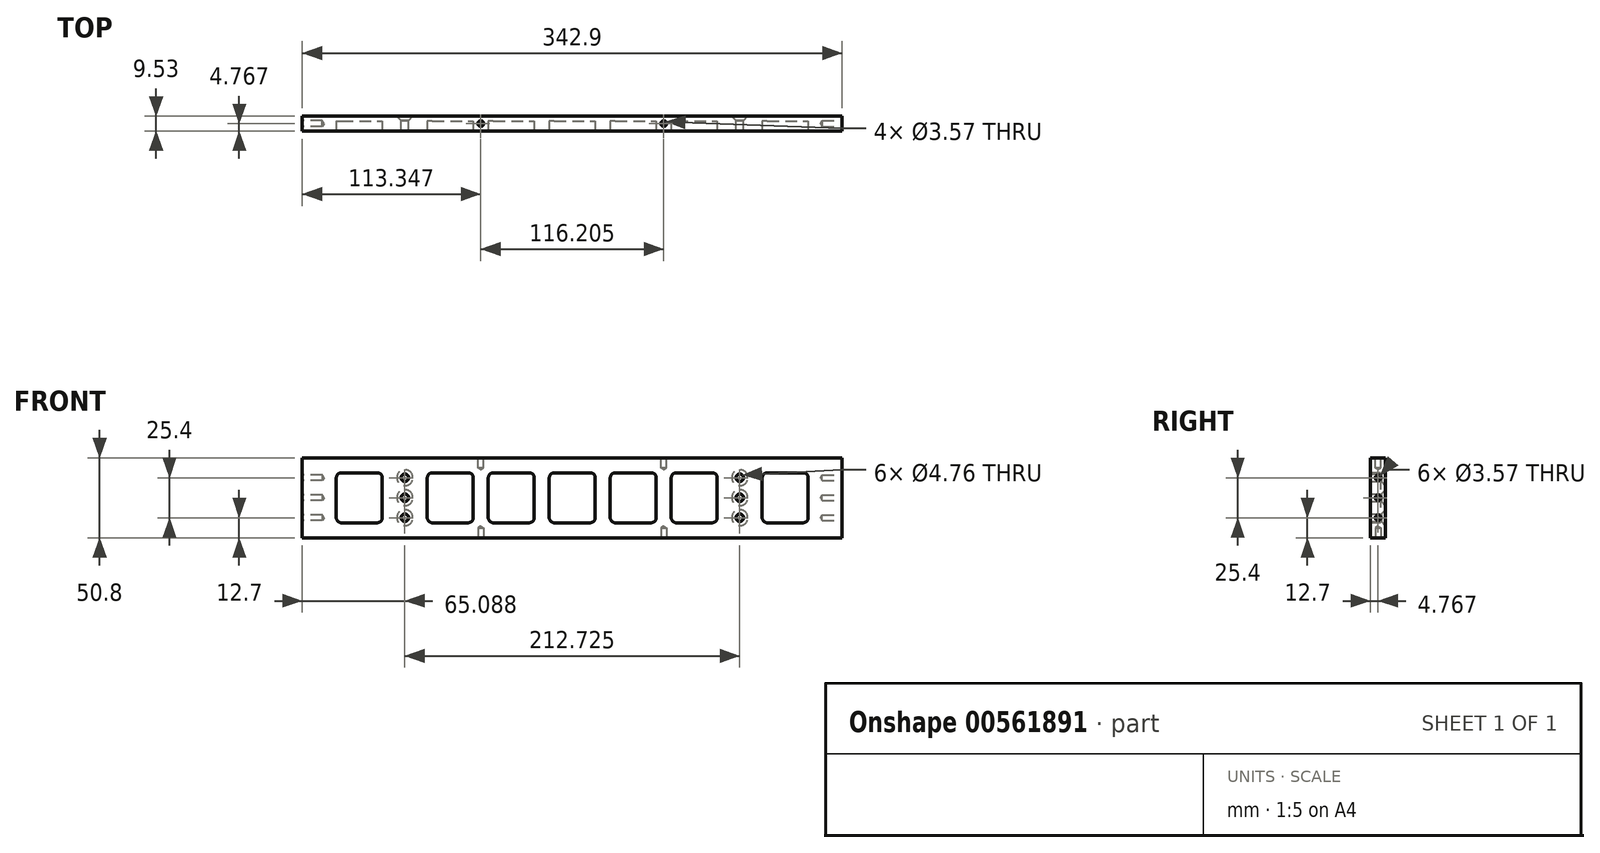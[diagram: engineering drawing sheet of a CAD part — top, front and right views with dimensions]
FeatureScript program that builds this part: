
annotation { "Feature Type Name" : "Feature", "Feature Type Description" : "" }
export const myFeature = defineFeature(function(context is Context, id is Id, definition is map)
    precondition{}
    {
        {
            var Q0;
            Q0=qCreatedBy(makeId("Front.planeOp"),FACE);
            var sketch = newSketch(context, id + "F0", { "sketchPlane" : qUnion([Q0])});
            skLineSegment(sketch, "E0", {"start": v(0, 0) * mm, "end": v(342.9, 0) * mm});
            skLineSegment(sketch, "E1", {"start": v(342.9, 0) * mm, "end": v(342.9, 50.8) * mm});
            skLineSegment(sketch, "E2", {"start": v(0, 0) * mm, "end": v(0, 50.8) * mm});
            skLineSegment(sketch, "E3", {"start": v(0, 50.8) * mm, "end": v(342.9, 50.8) * mm});
            skLineSegment(sketch, "E4", {"start": v(65.09, 50.8) * mm, "end": v(65.09, 0) * mm, "construction": true});
            skLineSegment(sketch, "E5", {"start": v(277.81, 50.8) * mm, "end": v(277.81, 0) * mm, "construction": true});
            skPoint(sketch, "E6", {"position": v(65.09, 25.4) * mm});
            skPoint(sketch, "E7", {"position": v(65.09, 38.1) * mm});
            skPoint(sketch, "E8", {"position": v(65.09, 12.7) * mm});
            skPoint(sketch, "E9", {"position": v(277.81, 25.4) * mm});
            skPoint(sketch, "E10", {"position": v(277.81, 38.1) * mm});
            skPoint(sketch, "E11", {"position": v(277.81, 12.7) * mm});
            skLineSegment(sketch, "E12", {"start": v(65.09, 38.1) * mm, "end": v(277.81, 38.1) * mm, "construction": true});
            skLineSegment(sketch, "E13", {"start": v(65.09, 12.7) * mm, "end": v(277.81, 12.7) * mm, "construction": true});
            skLineSegment(sketch, "E14", {"start": v(65.09, 25.4) * mm, "end": v(277.81, 25.4) * mm, "construction": true});
            skLineSegment(sketch, "E15", {"start": v(65.09, 25.4) * mm, "end": v(0, 25.4) * mm, "construction": true});
            skLineSegment(sketch, "E16", {"start": v(277.81, 25.4) * mm, "end": v(342.9, 25.4) * mm, "construction": true});
            skSolve(sketch);
        }
        {
            var Q0;
            Q0=makeQuery(id+"F0.imprint","IMPRINT",FACE,{"disambiguationData":[TD([[makeQuery(id+"F0.imprint","IMPRINT",EDGE,{"derivedFrom":sQuery(id+"F0.wireOp",EDGE,"E0")}),1.0]])]});
            extrude(context, id + "F1", {"entities" : qUnion([Q0]), "depth" : 9.52 * mm, "offsetDistance" : 25.4 * mm});
        }
        {
            var Q0;
            Q0=sQuery(id+"F0.wireOp",VERTEX,"E7");
            var Q1;
            Q1=sQuery(id+"F0.wireOp",VERTEX,"E6");
            var Q2;
            Q2=sQuery(id+"F0.wireOp",VERTEX,"E8");
            var Q3;
            Q3=sQuery(id+"F0.wireOp",VERTEX,"E10");
            var Q4;
            Q4=sQuery(id+"F0.wireOp",VERTEX,"E9");
            var Q5;
            Q5=sQuery(id+"F0.wireOp",VERTEX,"E11");
            var Q6;
            Q6=makeQuery(id+"F1.opExtrude","SWEPT_BODY",BODY,{"disambiguationData":[OSD([sQuery(id+"F0.wireOp",EDGE,"E0"),sQuery(id+"F0.wireOp",EDGE,"E1"),sQuery(id+"F0.wireOp",EDGE,"E2"),sQuery(id+"F0.wireOp",EDGE,"E3")])]});
            hole(context, id + "F2", {"style" : HoleStyle.C_SINK, "endStyle" : HoleEndStyle.THROUGH, "oppositeDirection" : true, "holeDiameter" : 4.76 * mm, "cSinkDiameter" : 10.16 * mm, "cSinkAngle" : 90 * degree, "majorDiameter" : 6.35 * mm, "isTappedThrough" : true, "tappedDepth" : 12.7 * mm, "tapClearance" : 3, "startFromSketch" : true, "locations" : qUnion([Q0, Q1, Q2, Q3, Q4, Q5]), "scope" : qUnion([Q6])});
        }
        {
            var Q0;
            Q0=makeQuery(id+"F1.opExtrude","SWEPT_FACE",FACE,{"disambiguationData":[OSD([sQuery(id+"F0.wireOp",EDGE,"E2")])]});
            var sketch = newSketch(context, id + "F3", { "sketchPlane" : qUnion([Q0])});
            skLineSegment(sketch, "E17", {"start": v(4.76, 50.8) * mm, "end": v(4.76, 0) * mm, "construction": true});
            skPoint(sketch, "E18", {"position": v(4.76, 25.4) * mm});
            skPoint(sketch, "E19", {"position": v(4.76, 38.1) * mm});
            skPoint(sketch, "E20", {"position": v(4.76, 12.7) * mm});
            skSolve(sketch);
        }
        {
            var Q0;
            Q0=sQuery(id+"F3.wireOp",VERTEX,"ff8bbe56-8198-4885-9724-5185ff2736ce");
            var Q1;
            Q1=sQuery(id+"F3.wireOp",VERTEX,"244a0df0-bff4-4081-86ab-2a0dd55871df");
            var Q2;
            Q2=sQuery(id+"F3.wireOp",VERTEX,"E18");
            var Q3;
            Q3=sQuery(id+"F3.wireOp",VERTEX,"E20");
            var Q4;
            Q4=sQuery(id+"F3.wireOp",VERTEX,"E19");
            var Q5;
            Q5=makeQuery(id+"F1.opExtrude","SWEPT_BODY",BODY,{"disambiguationData":[OSD([sQuery(id+"F0.wireOp",EDGE,"E0"),sQuery(id+"F0.wireOp",EDGE,"E1"),sQuery(id+"F0.wireOp",EDGE,"E2"),sQuery(id+"F0.wireOp",EDGE,"E3")])]});
            hole(context, id + "F4", {"style" : HoleStyle.SIMPLE, "endStyle" : HoleEndStyle.BLIND, "holeDiameter" : 3.57 * mm, "majorDiameter" : 6.35 * mm, "holeDepth" : 12.7 * mm, "isTappedThrough" : true, "tappedDepth" : 12.7 * mm, "tapClearance" : 3, "startFromSketch" : true, "locations" : qUnion([Q0, Q1, Q2, Q3, Q4]), "scope" : qUnion([Q5])});
        }
        {
            var Q0;
            Q0=makeQuery(id+"F1.opExtrude","SWEPT_FACE",FACE,{"disambiguationData":[OSD([sQuery(id+"F0.wireOp",EDGE,"E1")])]});
            var sketch = newSketch(context, id + "F5", { "sketchPlane" : qUnion([Q0])});
            skLineSegment(sketch, "E21", {"start": v(-4.76, 50.8) * mm, "end": v(-4.76, 0) * mm, "construction": true});
            skPoint(sketch, "E22", {"position": v(-4.76, 25.4) * mm});
            skPoint(sketch, "E23", {"position": v(-4.76, 38.1) * mm});
            skPoint(sketch, "E24", {"position": v(-4.76, 12.7) * mm});
            skSolve(sketch);
        }
        {
            var Q0;
            Q0=sQuery(id+"F5.wireOp",VERTEX,"f5ca80d4-63bc-4319-a2d7-8be359f209f6");
            var Q1;
            Q1=sQuery(id+"F5.wireOp",VERTEX,"8e91c998-63aa-4cf8-b9d6-40a529184d54");
            var Q2;
            Q2=sQuery(id+"F5.wireOp",VERTEX,"E24");
            var Q3;
            Q3=sQuery(id+"F5.wireOp",VERTEX,"E22");
            var Q4;
            Q4=sQuery(id+"F5.wireOp",VERTEX,"E23");
            var Q5;
            Q5=makeQuery(id+"F1.opExtrude","SWEPT_BODY",BODY,{"disambiguationData":[OSD([sQuery(id+"F0.wireOp",EDGE,"E0"),sQuery(id+"F0.wireOp",EDGE,"E1"),sQuery(id+"F0.wireOp",EDGE,"E2"),sQuery(id+"F0.wireOp",EDGE,"E3")])]});
            hole(context, id + "F6", {"style" : HoleStyle.SIMPLE, "endStyle" : HoleEndStyle.BLIND, "holeDiameter" : 3.57 * mm, "majorDiameter" : 6.35 * mm, "holeDepth" : 12.7 * mm, "isTappedThrough" : true, "tappedDepth" : 12.7 * mm, "tapClearance" : 3, "startFromSketch" : true, "locations" : qUnion([Q0, Q1, Q2, Q3, Q4]), "scope" : qUnion([Q5])});
        }
        {
            var Q0;
            Q0=makeQuery(id+"F1.opExtrude","CAP_FACE",FACE,{"disambiguationData":[OSD([sQuery(id+"F0.wireOp",EDGE,"E0"),sQuery(id+"F0.wireOp",EDGE,"E1"),sQuery(id+"F0.wireOp",EDGE,"E2"),sQuery(id+"F0.wireOp",EDGE,"E3")])],"isStart":false});
            var sketch = newSketch(context, id + "F7", { "sketchPlane" : qUnion([Q0])});
            skLineSegment(sketch, "E25.bottom", {"start": v(79.37, 41.27) * mm, "end": v(263.53, 41.27) * mm});
            skLineSegment(sketch, "E25.top", {"start": v(79.37, 9.52) * mm, "end": v(263.53, 9.52) * mm});
            skLineSegment(sketch, "E25.left", {"start": v(79.37, 41.27) * mm, "end": v(79.37, 9.52) * mm});
            skLineSegment(sketch, "E25.right", {"start": v(263.53, 41.27) * mm, "end": v(263.53, 9.52) * mm});
            skLineSegment(sketch, "E26", {"start": v(108.58, 41.27) * mm, "end": v(108.58, 9.52) * mm});
            skLineSegment(sketch, "E27", {"start": v(118.1, 41.27) * mm, "end": v(118.1, 9.52) * mm});
            skLineSegment(sketch, "E28", {"start": v(147.32, 41.27) * mm, "end": v(147.32, 9.52) * mm});
            skLineSegment(sketch, "E29", {"start": v(156.84, 41.27) * mm, "end": v(156.84, 9.52) * mm});
            skLineSegment(sketch, "E30", {"start": v(186.05, 41.27) * mm, "end": v(186.05, 9.52) * mm});
            skLineSegment(sketch, "E31", {"start": v(195.58, 41.27) * mm, "end": v(195.58, 9.52) * mm});
            skLineSegment(sketch, "E32", {"start": v(224.79, 41.27) * mm, "end": v(224.79, 9.52) * mm});
            skLineSegment(sketch, "E33", {"start": v(234.31, 41.27) * mm, "end": v(234.31, 9.52) * mm});
            skLineSegment(sketch, "E34", {"start": v(79.37, 9.52) * mm, "end": v(65.09, 12.7) * mm});
            skLineSegment(sketch, "E35", {"start": v(79.37, 41.27) * mm, "end": v(65.09, 38.1) * mm, "construction": true});
            skLineSegment(sketch, "E36", {"start": v(277.81, 38.1) * mm, "end": v(263.53, 41.27) * mm, "construction": true});
            skLineSegment(sketch, "E37", {"start": v(277.81, 12.7) * mm, "end": v(263.53, 9.52) * mm, "construction": true});
            skLineSegment(sketch, "E38.bottom", {"start": v(21.6, 41.27) * mm, "end": v(50.8, 41.27) * mm});
            skLineSegment(sketch, "E38.top", {"start": v(21.6, 9.52) * mm, "end": v(50.8, 9.52) * mm});
            skLineSegment(sketch, "E38.left", {"start": v(21.6, 41.27) * mm, "end": v(21.6, 9.52) * mm});
            skLineSegment(sketch, "E38.right", {"start": v(50.8, 41.27) * mm, "end": v(50.8, 9.52) * mm});
            skLineSegment(sketch, "E39.bottom", {"start": v(292.1, 41.27) * mm, "end": v(321.31, 41.27) * mm});
            skLineSegment(sketch, "E39.top", {"start": v(292.1, 9.52) * mm, "end": v(321.31, 9.52) * mm});
            skLineSegment(sketch, "E39.left", {"start": v(292.1, 41.27) * mm, "end": v(292.1, 9.52) * mm});
            skLineSegment(sketch, "E39.right", {"start": v(321.31, 41.27) * mm, "end": v(321.31, 9.52) * mm});
            skLineSegment(sketch, "E40", {"start": v(263.53, 41.27) * mm, "end": v(292.1, 41.27) * mm, "construction": true});
            skLineSegment(sketch, "E41", {"start": v(79.37, 41.27) * mm, "end": v(50.8, 41.27) * mm, "construction": true});
            skSolve(sketch);
        }
        {
            var Q0;
            {var subQ0=sQuery(id+"F7.wireOp",EDGE,"E25.left");Q0=makeQuery(id+"F7.imprint","IMPRINT",FACE,{"disambiguationData":[TD([[makeQuery(id+"F7.imprint","IMPRINT",EDGE,{"derivedFrom":subQ0}),1.0]])]});}
            var Q1;
            {var subQ0=sQuery(id+"F7.wireOp",EDGE,"E27");Q1=makeQuery(id+"F7.imprint","IMPRINT",FACE,{"disambiguationData":[TD([[makeQuery(id+"F7.imprint","IMPRINT",EDGE,{"derivedFrom":subQ0}),1.0]])]});}
            var Q2;
            {var subQ0=sQuery(id+"F7.wireOp",EDGE,"E29");Q2=makeQuery(id+"F7.imprint","IMPRINT",FACE,{"disambiguationData":[TD([[makeQuery(id+"F7.imprint","IMPRINT",EDGE,{"derivedFrom":subQ0}),1.0]])]});}
            var Q3;
            {var subQ0=sQuery(id+"F7.wireOp",EDGE,"E31");Q3=makeQuery(id+"F7.imprint","IMPRINT",FACE,{"disambiguationData":[TD([[makeQuery(id+"F7.imprint","IMPRINT",EDGE,{"derivedFrom":subQ0}),1.0]])]});}
            var Q4;
            {var subQ0=sQuery(id+"F7.wireOp",EDGE,"E25.right");Q4=makeQuery(id+"F7.imprint","IMPRINT",FACE,{"disambiguationData":[TD([[makeQuery(id+"F7.imprint","IMPRINT",EDGE,{"derivedFrom":subQ0}),-1.0]])]});}
            var Q5;
            Q5=makeQuery(id+"F7.imprint","IMPRINT",FACE,{"disambiguationData":[TD([[makeQuery(id+"F7.imprint","IMPRINT",EDGE,{"derivedFrom":sQuery(id+"F7.wireOp",EDGE,"E38.bottom")}),-1.0]])]});
            var Q6;
            Q6=makeQuery(id+"F7.imprint","IMPRINT",FACE,{"disambiguationData":[TD([[makeQuery(id+"F7.imprint","IMPRINT",EDGE,{"derivedFrom":sQuery(id+"F7.wireOp",EDGE,"E39.bottom")}),-1.0]])]});
            extrude(context, id + "F8", {"entities" : qUnion([Q0, Q1, Q2, Q3, Q4, Q5, Q6]), "operationType" : NewBodyOperationType.REMOVE, "oppositeDirection" : true, "depth" : 6.35 * mm, "offsetDistance" : 25.4 * mm});
        }
        {
            var Q0;
            Q0=makeQuery(id+"F8.boolean.opBoolean","COPY",EDGE,{"derivedFrom":makeQuery(id+"F8.opExtrude","SWEPT_EDGE",EDGE,{"disambiguationData":[OSD([sQuery(id+"F7.wireOp",EDGE,"E25.bottom"),sQuery(id+"F7.wireOp",EDGE,"E29")])]})});
            var Q1;
            Q1=makeQuery(id+"F8.boolean.opBoolean","COPY",EDGE,{"derivedFrom":makeQuery(id+"F8.opExtrude","SWEPT_EDGE",EDGE,{"disambiguationData":[OSD([sQuery(id+"F7.wireOp",EDGE,"E25.bottom"),sQuery(id+"F7.wireOp",EDGE,"E31")])]})});
            var Q2;
            Q2=makeQuery(id+"F8.boolean.opBoolean","COPY",EDGE,{"derivedFrom":makeQuery(id+"F8.opExtrude","SWEPT_EDGE",EDGE,{"disambiguationData":[OSD([sQuery(id+"F7.wireOp",EDGE,"E25.bottom"),sQuery(id+"F7.wireOp",EDGE,"E33")])]})});
            var Q3;
            Q3=makeQuery(id+"F8.boolean.opBoolean","COPY",EDGE,{"derivedFrom":makeQuery(id+"F8.opExtrude","SWEPT_EDGE",EDGE,{"disambiguationData":[OSD([sQuery(id+"F7.wireOp",EDGE,"E25.bottom"),sQuery(id+"F7.wireOp",EDGE,"E25.left")])]})});
            var Q4;
            Q4=makeQuery(id+"F8.boolean.opBoolean","COPY",EDGE,{"derivedFrom":makeQuery(id+"F8.opExtrude","SWEPT_EDGE",EDGE,{"disambiguationData":[OSD([sQuery(id+"F7.wireOp",EDGE,"E25.bottom"),sQuery(id+"F7.wireOp",EDGE,"E27")])]})});
            var Q5;
            Q5=makeQuery(id+"F8.boolean.opBoolean","COPY",EDGE,{"derivedFrom":makeQuery(id+"F8.opExtrude","SWEPT_EDGE",EDGE,{"disambiguationData":[OSD([sQuery(id+"F7.wireOp",EDGE,"E25.top"),sQuery(id+"F7.wireOp",EDGE,"E25.left")])]})});
            var Q6;
            Q6=makeQuery(id+"F8.boolean.opBoolean","COPY",EDGE,{"derivedFrom":makeQuery(id+"F8.opExtrude","SWEPT_EDGE",EDGE,{"disambiguationData":[OSD([sQuery(id+"F7.wireOp",EDGE,"E25.top"),sQuery(id+"F7.wireOp",EDGE,"E27")])]})});
            var Q7;
            Q7=makeQuery(id+"F8.boolean.opBoolean","COPY",EDGE,{"derivedFrom":makeQuery(id+"F8.opExtrude","SWEPT_EDGE",EDGE,{"disambiguationData":[OSD([sQuery(id+"F7.wireOp",EDGE,"E25.top"),sQuery(id+"F7.wireOp",EDGE,"E29")])]})});
            var Q8;
            Q8=makeQuery(id+"F8.boolean.opBoolean","COPY",EDGE,{"derivedFrom":makeQuery(id+"F8.opExtrude","SWEPT_EDGE",EDGE,{"disambiguationData":[OSD([sQuery(id+"F7.wireOp",EDGE,"E25.top"),sQuery(id+"F7.wireOp",EDGE,"E31")])]})});
            var Q9;
            Q9=makeQuery(id+"F8.boolean.opBoolean","COPY",EDGE,{"derivedFrom":makeQuery(id+"F8.opExtrude","SWEPT_EDGE",EDGE,{"disambiguationData":[OSD([sQuery(id+"F7.wireOp",EDGE,"E25.top"),sQuery(id+"F7.wireOp",EDGE,"E33")])]})});
            var Q10;
            Q10=makeQuery(id+"F8.boolean.opBoolean","COPY",EDGE,{"derivedFrom":makeQuery(id+"F8.opExtrude","SWEPT_EDGE",EDGE,{"disambiguationData":[OSD([sQuery(id+"F7.wireOp",EDGE,"E25.bottom"),sQuery(id+"F7.wireOp",EDGE,"E26")])]})});
            var Q11;
            Q11=makeQuery(id+"F8.boolean.opBoolean","COPY",EDGE,{"derivedFrom":makeQuery(id+"F8.opExtrude","SWEPT_EDGE",EDGE,{"disambiguationData":[OSD([sQuery(id+"F7.wireOp",EDGE,"E25.bottom"),sQuery(id+"F7.wireOp",EDGE,"E28")])]})});
            var Q12;
            Q12=makeQuery(id+"F8.boolean.opBoolean","COPY",EDGE,{"derivedFrom":makeQuery(id+"F8.opExtrude","SWEPT_EDGE",EDGE,{"disambiguationData":[OSD([sQuery(id+"F7.wireOp",EDGE,"E25.bottom"),sQuery(id+"F7.wireOp",EDGE,"E30")])]})});
            var Q13;
            Q13=makeQuery(id+"F8.boolean.opBoolean","COPY",EDGE,{"derivedFrom":makeQuery(id+"F8.opExtrude","SWEPT_EDGE",EDGE,{"disambiguationData":[OSD([sQuery(id+"F7.wireOp",EDGE,"E25.bottom"),sQuery(id+"F7.wireOp",EDGE,"E32")])]})});
            var Q14;
            Q14=makeQuery(id+"F8.boolean.opBoolean","COPY",EDGE,{"derivedFrom":makeQuery(id+"F8.opExtrude","SWEPT_EDGE",EDGE,{"disambiguationData":[OSD([sQuery(id+"F7.wireOp",EDGE,"E25.bottom"),sQuery(id+"F7.wireOp",EDGE,"E25.right")])]})});
            var Q15;
            Q15=makeQuery(id+"F8.boolean.opBoolean","COPY",EDGE,{"derivedFrom":makeQuery(id+"F8.opExtrude","SWEPT_EDGE",EDGE,{"disambiguationData":[OSD([sQuery(id+"F7.wireOp",EDGE,"E25.top"),sQuery(id+"F7.wireOp",EDGE,"E25.right")])]})});
            var Q16;
            Q16=makeQuery(id+"F8.boolean.opBoolean","COPY",EDGE,{"derivedFrom":makeQuery(id+"F8.opExtrude","SWEPT_EDGE",EDGE,{"disambiguationData":[OSD([sQuery(id+"F7.wireOp",EDGE,"E25.top"),sQuery(id+"F7.wireOp",EDGE,"E32")])]})});
            var Q17;
            Q17=makeQuery(id+"F8.boolean.opBoolean","COPY",EDGE,{"derivedFrom":makeQuery(id+"F8.opExtrude","SWEPT_EDGE",EDGE,{"disambiguationData":[OSD([sQuery(id+"F7.wireOp",EDGE,"E25.top"),sQuery(id+"F7.wireOp",EDGE,"E30")])]})});
            var Q18;
            Q18=makeQuery(id+"F8.boolean.opBoolean","COPY",EDGE,{"derivedFrom":makeQuery(id+"F8.opExtrude","SWEPT_EDGE",EDGE,{"disambiguationData":[OSD([sQuery(id+"F7.wireOp",EDGE,"E25.top"),sQuery(id+"F7.wireOp",EDGE,"E28")])]})});
            var Q19;
            Q19=makeQuery(id+"F8.boolean.opBoolean","COPY",EDGE,{"derivedFrom":makeQuery(id+"F8.opExtrude","SWEPT_EDGE",EDGE,{"disambiguationData":[OSD([sQuery(id+"F7.wireOp",EDGE,"E25.top"),sQuery(id+"F7.wireOp",EDGE,"E26")])]})});
            var Q20;
            Q20=makeQuery(id+"F8.boolean.opBoolean","COPY",EDGE,{"derivedFrom":makeQuery(id+"F8.opExtrude","SWEPT_EDGE",EDGE,{"disambiguationData":[OSD([sQuery(id+"F7.wireOp",EDGE,"E39.bottom"),sQuery(id+"F7.wireOp",EDGE,"E39.right")])]})});
            var Q21;
            Q21=makeQuery(id+"F8.boolean.opBoolean","COPY",EDGE,{"derivedFrom":makeQuery(id+"F8.opExtrude","SWEPT_EDGE",EDGE,{"disambiguationData":[OSD([sQuery(id+"F7.wireOp",EDGE,"E39.bottom"),sQuery(id+"F7.wireOp",EDGE,"E39.left")])]})});
            var Q22;
            Q22=makeQuery(id+"F8.boolean.opBoolean","COPY",EDGE,{"derivedFrom":makeQuery(id+"F8.opExtrude","SWEPT_EDGE",EDGE,{"disambiguationData":[OSD([sQuery(id+"F7.wireOp",EDGE,"E39.top"),sQuery(id+"F7.wireOp",EDGE,"E39.left")])]})});
            var Q23;
            Q23=makeQuery(id+"F8.boolean.opBoolean","COPY",EDGE,{"derivedFrom":makeQuery(id+"F8.opExtrude","SWEPT_EDGE",EDGE,{"disambiguationData":[OSD([sQuery(id+"F7.wireOp",EDGE,"E39.top"),sQuery(id+"F7.wireOp",EDGE,"E39.right")])]})});
            var Q24;
            Q24=makeQuery(id+"F8.boolean.opBoolean","COPY",EDGE,{"derivedFrom":makeQuery(id+"F8.opExtrude","SWEPT_EDGE",EDGE,{"disambiguationData":[OSD([sQuery(id+"F7.wireOp",EDGE,"E38.top"),sQuery(id+"F7.wireOp",EDGE,"E38.right")])]})});
            var Q25;
            Q25=makeQuery(id+"F8.boolean.opBoolean","COPY",EDGE,{"derivedFrom":makeQuery(id+"F8.opExtrude","SWEPT_EDGE",EDGE,{"disambiguationData":[OSD([sQuery(id+"F7.wireOp",EDGE,"E38.bottom"),sQuery(id+"F7.wireOp",EDGE,"E38.right")])]})});
            var Q26;
            Q26=makeQuery(id+"F8.boolean.opBoolean","COPY",EDGE,{"derivedFrom":makeQuery(id+"F8.opExtrude","SWEPT_EDGE",EDGE,{"disambiguationData":[OSD([sQuery(id+"F7.wireOp",EDGE,"E38.bottom"),sQuery(id+"F7.wireOp",EDGE,"E38.left")])]})});
            var Q27;
            Q27=makeQuery(id+"F8.boolean.opBoolean","COPY",EDGE,{"derivedFrom":makeQuery(id+"F8.opExtrude","SWEPT_EDGE",EDGE,{"disambiguationData":[OSD([sQuery(id+"F7.wireOp",EDGE,"E38.top"),sQuery(id+"F7.wireOp",EDGE,"E38.left")])]})});
            fillet(context, id + "F9", {"entities" : qUnion([Q0, Q1, Q2, Q3, Q4, Q5, Q6, Q7, Q8, Q9, Q10, Q11, Q12, Q13, Q14, Q15, Q16, Q17, Q18, Q19, Q20, Q21, Q22, Q23, Q24, Q25, Q26, Q27]), "radius" : 3.17 * mm, "tangentPropagation" : true, "allowEdgeOverflow" : false});
        }
        {
            var Q0;
            Q0=makeQuery(id+"F1.opExtrude","SWEPT_FACE",FACE,{"disambiguationData":[OSD([sQuery(id+"F0.wireOp",EDGE,"E0")])]});
            var sketch = newSketch(context, id + "F10", { "sketchPlane" : qUnion([Q0])});
            skLineSegment(sketch, "E42", {"start": v(113.35, 9.53) * mm, "end": v(113.35, 0) * mm});
            skLineSegment(sketch, "E43", {"start": v(229.55, 9.53) * mm, "end": v(229.55, 0) * mm});
            skPoint(sketch, "E44", {"position": v(113.35, 4.76) * mm});
            skPoint(sketch, "E45", {"position": v(229.55, 4.76) * mm});
            skSolve(sketch);
        }
        {
            var Q0;
            Q0=makeQuery(id+"F1.opExtrude","SWEPT_FACE",FACE,{"disambiguationData":[OSD([sQuery(id+"F0.wireOp",EDGE,"E3")])]});
            var sketch = newSketch(context, id + "F11", { "sketchPlane" : qUnion([Q0])});
            skLineSegment(sketch, "E46", {"start": v(113.35, 0) * mm, "end": v(113.35, -9.53) * mm});
            skLineSegment(sketch, "E47", {"start": v(229.55, 0) * mm, "end": v(229.55, -9.53) * mm});
            skPoint(sketch, "E48", {"position": v(229.55, -4.76) * mm});
            skPoint(sketch, "E49", {"position": v(113.35, -4.76) * mm});
            skSolve(sketch);
        }
        {
            var Q0;
            Q0=sQuery(id+"F11.wireOp",VERTEX,"E48");
            var Q1;
            Q1=sQuery(id+"F11.wireOp",VERTEX,"E49");
            var Q2;
            Q2=sQuery(id+"F10.wireOp",VERTEX,"E44");
            var Q3;
            Q3=sQuery(id+"F10.wireOp",VERTEX,"E45");
            var Q4;
            Q4=makeQuery(id+"F1.opExtrude","SWEPT_BODY",BODY,{"disambiguationData":[OSD([sQuery(id+"F0.wireOp",EDGE,"E0"),sQuery(id+"F0.wireOp",EDGE,"E1"),sQuery(id+"F0.wireOp",EDGE,"E2"),sQuery(id+"F0.wireOp",EDGE,"E3")])]});
            hole(context, id + "F12", {"style" : HoleStyle.SIMPLE, "endStyle" : HoleEndStyle.BLIND, "holeDiameter" : 3.57 * mm, "majorDiameter" : 6.35 * mm, "holeDepth" : 6.35 * mm, "isTappedThrough" : true, "tappedDepth" : 12.7 * mm, "tapClearance" : 3, "startFromSketch" : true, "locations" : qUnion([Q0, Q1, Q2, Q3]), "scope" : qUnion([Q4])});
        }
    });
